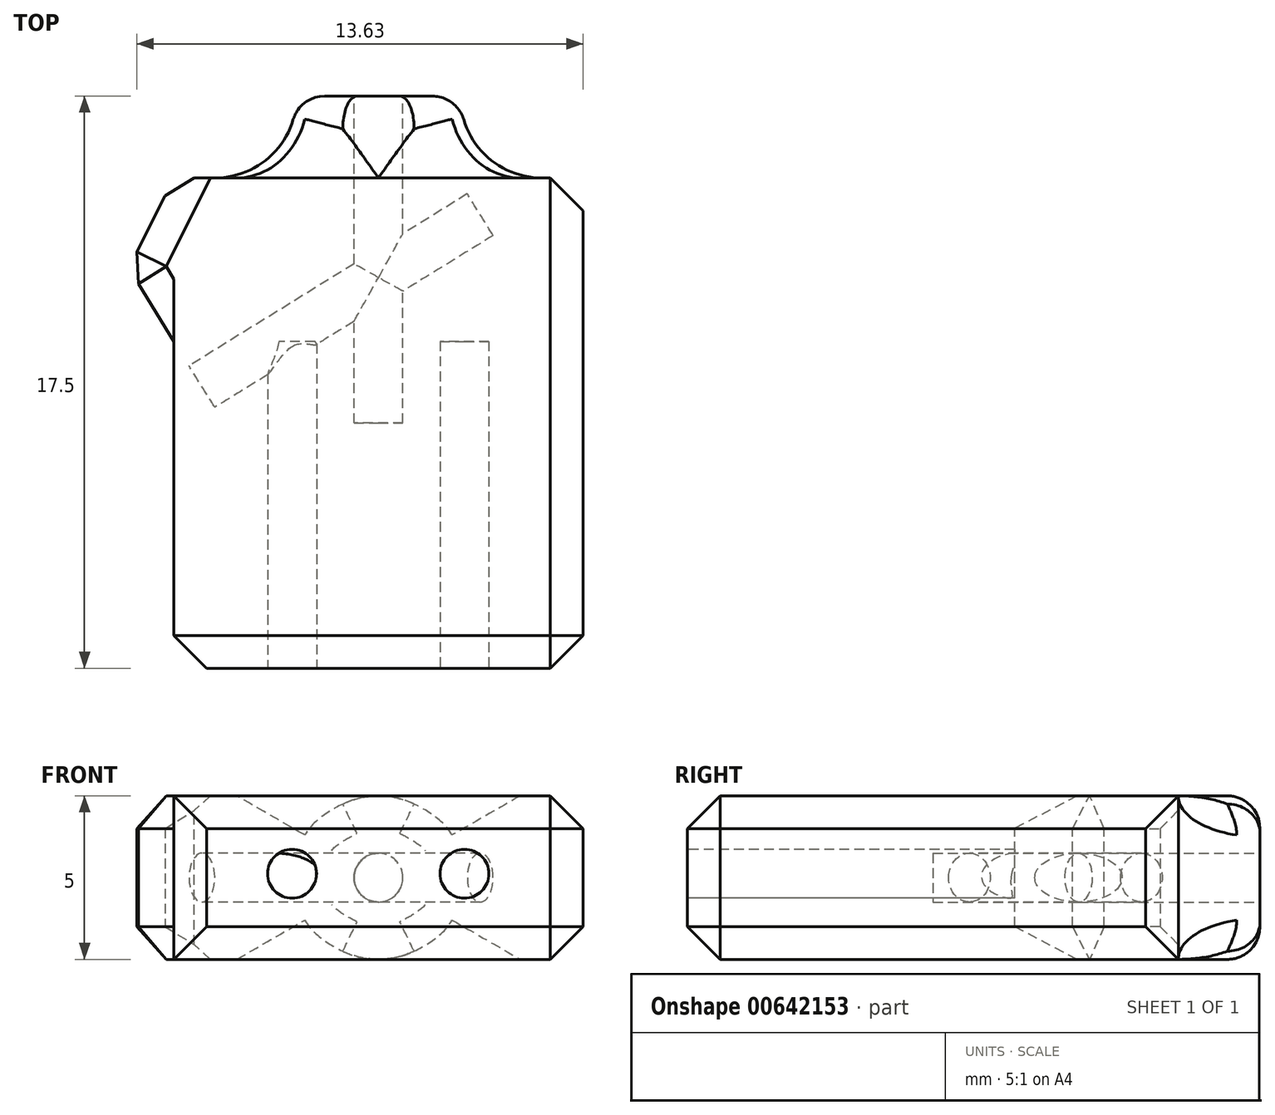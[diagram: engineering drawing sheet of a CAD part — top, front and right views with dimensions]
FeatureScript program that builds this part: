
annotation { "Feature Type Name" : "Feature", "Feature Type Description" : "" }
export const myFeature = defineFeature(function(context is Context, id is Id, definition is map)
    precondition{}
    {
        {
            var Q0;
            Q0=qCreatedBy(makeId("Top.planeOp"),FACE);
            var sketch = newSketch(context, id + "F0", { "sketchPlane" : qUnion([Q0])});
            skLineSegment(sketch, "E0.bottom", {"start": v(-3.03, 3.08) * mm, "end": v(9.47, 3.08) * mm});
            skLineSegment(sketch, "E0.top", {"start": v(-3.03, -11.92) * mm, "end": v(9.47, -11.92) * mm});
            skLineSegment(sketch, "E0.left", {"start": v(-3.03, 3.08) * mm, "end": v(-3.03, -11.92) * mm});
            skLineSegment(sketch, "E0.right", {"start": v(9.47, 3.08) * mm, "end": v(9.47, -11.92) * mm});
            skLineSegment(sketch, "E1.top", {"start": v(-3.03, -6.92) * mm, "end": v(-8.03, -6.92) * mm});
            skLineSegment(sketch, "E1.left", {"start": v(-3.03, -11.92) * mm, "end": v(-3.03, -6.92) * mm});
            skLineSegment(sketch, "E2", {"start": v(-8.03, -6.92) * mm, "end": v(-3.03, 3.08) * mm});
            skLineSegment(sketch, "E3", {"start": v(-8.03, -6.92) * mm, "end": v(-3.03, -6.92) * mm});
            skSolve(sketch);
        }
        {
            var Q0;
            Q0=makeQuery(id+"F0.imprint","IMPRINT",FACE,{"disambiguationData":[TD([[makeQuery(id+"F0.imprint","IMPRINT",EDGE,{"derivedFrom":sQuery(id+"F0.wireOp",EDGE,"E0.left")}),-1.0]])]});
            var Q1;
            Q1=makeQuery(id+"F0.imprint","IMPRINT",FACE,{"disambiguationData":[TD([[makeQuery(id+"F0.imprint","IMPRINT",EDGE,{"derivedFrom":sQuery(id+"F0.wireOp",EDGE,"E0.bottom")}),-1.0]])]});
            extrude(context, id + "F1", {"entities" : qUnion([Q0, Q1]), "depth" : 5 * mm, "offsetDistance" : 25.4 * mm});
        }
        {
            var Q0;
            Q0=makeQuery(id+"F1.opExtrude","SWEPT_EDGE",EDGE,{"disambiguationData":[OSD([sQuery(id+"F0.wireOp",EDGE,"E2"),sQuery(id+"F0.wireOp",EDGE,"E3")])]});
            chamfer(context, id + "F2", {"entities" : qUnion([Q0]), "width" : 5 * mm, "tangentPropagation" : true});
        }
        {
            var Q0;
            Q0=makeQuery(id+"F2.opChamfer","BLEND_FACE",FACE,{"disambiguationData":[OSD([sQuery(id+"F0.wireOp",EDGE,"E2"),sQuery(id+"F0.wireOp",EDGE,"E3")])]});
            var sketch = newSketch(context, id + "F3", { "sketchPlane" : qUnion([Q0])});
            skCircle(sketch, "E4", {"center": v(1.67, 2.5) * mm, "radius": 0.75 * mm});
            skPoint(sketch, "E4.centerSnap0", {"position": v(-0.96, 2.5) * mm});
            skPoint(sketch, "E4.centerSnap1", {"position": v(1.67, 0) * mm});
            skSolve(sketch);
        }
        {
            var Q0;
            Q0=makeQuery(id+"F1.opExtrude","SWEPT_FACE",FACE,{"disambiguationData":[OSD([sQuery(id+"F0.wireOp",EDGE,"E0.top")])]});
            var sketch = newSketch(context, id + "F4", { "sketchPlane" : qUnion([Q0])});
            skSolve(sketch);
        }
        {
            var Q0;
            Q0=makeQuery(id+"F1.opExtrude","SWEPT_FACE",FACE,{"disambiguationData":[OSD([sQuery(id+"F0.wireOp",EDGE,"E0.bottom")])]});
            var sketch = newSketch(context, id + "F5", { "sketchPlane" : qUnion([Q0])});
            skCircle(sketch, "E5", {"center": v(-3.22, 2.5) * mm, "radius": 2.5 * mm});
            skPoint(sketch, "E5.centerSnap0", {"position": v(-9.47, 2.5) * mm});
            skPoint(sketch, "E5.centerSnap1", {"position": v(-3.22, 5) * mm});
            skSolve(sketch);
        }
        {
            var Q0;
            {var subQ0=sQuery(id+"F5.wireOp",EDGE,"E5");var subQ1=sQuery(id+"F0.wireOp",EDGE,"E0.bottom");var subQ2=makeQuery(id+"F5.imprint","INTERSECT",VERTEX,{"derivedFrom":[makeQuery(id+"F1.opExtrude","CAP_EDGE",EDGE,{"disambiguationData":[OSD([subQ1])],"isStart":true}),subQ0]});Q0=makeQuery(id+"F5.imprint","IMPRINT",FACE,{"disambiguationData":[TD([[makeQuery(id+"F5.imprint","IMPRINT",EDGE,{"disambiguationData":[TD([[subQ2,1.0]])],"derivedFrom":subQ0}),1.0]])]});}
            extrude(context, id + "F6", {"entities" : qUnion([Q0]), "operationType" : NewBodyOperationType.ADD, "depth" : 2.5 * mm, "offsetDistance" : 25.4 * mm});
        }
        {
            var Q0;
            Q0=makeQuery(id+"F6.boolean.opBoolean","SPLIT",EDGE,{"disambiguationData":[OD(1.0)],"derivedFrom":makeQuery(id+"F6.opExtrude","CAP_EDGE",EDGE,{"disambiguationData":[OSD([sQuery(id+"F5.wireOp",EDGE,"E5")])],"isStart":true})});
            fillet(context, id + "F7", {"entities" : qUnion([Q0]), "radius" : 2.5 * mm, "tangentPropagation" : true, "allowEdgeOverflow" : false});
        }
        {
            var Q0;
            Q0=makeQuery(id+"F6.opExtrude","CAP_EDGE",EDGE,{"disambiguationData":[OSD([sQuery(id+"F5.wireOp",EDGE,"E5")])],"isStart":false});
            var Q1;
            {var subQ0=sQuery(id+"F5.wireOp",EDGE,"E5");Q1=makeQuery(id+"F7.opFillet","BLEND_EDGE",EDGE,{"blendedFrom":[makeQuery(id+"F6.boolean.opBoolean","SPLIT",EDGE,{"disambiguationData":[OD(1.0)],"derivedFrom":makeQuery(id+"F6.opExtrude","CAP_EDGE",EDGE,{"disambiguationData":[OSD([subQ0])],"isStart":true})}),makeQuery(id+"F6.opExtrude","CAP_FACE",FACE,{"disambiguationData":[OSD([subQ0])],"isStart":false})],"blendedInto":[makeQuery(id+"F6.opExtrude","CAP_FACE",FACE,{"disambiguationData":[OSD([subQ0])],"isStart":false})]});}
            var Q2;
            {var subQ0=sQuery(id+"F5.wireOp",EDGE,"E5");Q2=makeQuery(id+"F7.opFillet","BLEND_EDGE",EDGE,{"blendedFrom":[makeQuery(id+"F6.boolean.opBoolean","SPLIT",EDGE,{"disambiguationData":[OD(0.0)],"derivedFrom":makeQuery(id+"F6.opExtrude","CAP_EDGE",EDGE,{"disambiguationData":[OSD([subQ0])],"isStart":true})}),makeQuery(id+"F6.opExtrude","CAP_FACE",FACE,{"disambiguationData":[OSD([subQ0])],"isStart":false})],"blendedInto":[makeQuery(id+"F6.opExtrude","CAP_FACE",FACE,{"disambiguationData":[OSD([subQ0])],"isStart":false})]});}
            fillet(context, id + "F8", {"entities" : qUnion([Q0, Q1, Q2]), "radius" : 1 * mm, "tangentPropagation" : true, "allowEdgeOverflow" : false});
        }
        {
            var Q0;
            Q0=makeQuery(id+"F6.opExtrude","CAP_FACE",FACE,{"disambiguationData":[OSD([sQuery(id+"F5.wireOp",EDGE,"E5")])],"isStart":false});
            var sketch = newSketch(context, id + "F9", { "sketchPlane" : qUnion([Q0])});
            skCircle(sketch, "E6", {"center": v(-3.22, 2.5) * mm, "radius": 0.75 * mm});
            skSolve(sketch);
        }
        {
            var Q0;
            Q0=makeQuery(id+"F3.imprint","IMPRINT",FACE,{"disambiguationData":[TD([[makeQuery(id+"F3.imprint","IMPRINT",EDGE,{"derivedFrom":sQuery(id+"F3.wireOp",EDGE,"E4")}),1.0]])]});
            var Q1;
            Q1=sQuery(id+"F3.wireOp",EDGE,"E4");
            extrude(context, id + "F10", {"entities" : qUnion([Q0]), "operationType" : NewBodyOperationType.REMOVE, "surfaceEntities" : qUnion([Q1]), "oppositeDirection" : true, "depth" : 10 * mm, "offsetDistance" : 25.4 * mm});
        }
        {
            var Q0;
            Q0=makeQuery(id+"F1.opExtrude","CAP_EDGE",EDGE,{"disambiguationData":[OSD([sQuery(id+"F0.wireOp",EDGE,"E0.top")])],"isStart":false});
            var Q1;
            Q1=makeQuery(id+"F1.opExtrude","CAP_EDGE",EDGE,{"disambiguationData":[OSD([sQuery(id+"F0.wireOp",EDGE,"E0.right")])],"isStart":false});
            var Q2;
            Q2=makeQuery(id+"F2.opChamfer","BLEND_EDGE",EDGE,{"blendedFrom":[makeQuery(id+"F1.opExtrude","SWEPT_EDGE",EDGE,{"disambiguationData":[OSD([sQuery(id+"F0.wireOp",EDGE,"E2"),sQuery(id+"F0.wireOp",EDGE,"E3")])]}),makeQuery(id+"F1.opExtrude","SWEPT_FACE",FACE,{"disambiguationData":[OSD([sQuery(id+"F0.wireOp",EDGE,"E1.left")])]})],"blendedInto":[makeQuery(id+"F1.opExtrude","SWEPT_FACE",FACE,{"disambiguationData":[OSD([sQuery(id+"F0.wireOp",EDGE,"E1.left")])]})]});
            var Q3;
            {var subQ0=sQuery(id+"F0.wireOp",EDGE,"E2");Q3=makeQuery(id+"F2.opChamfer","BLEND_EDGE",EDGE,{"blendedFrom":[makeQuery(id+"F1.opExtrude","SWEPT_EDGE",EDGE,{"disambiguationData":[OSD([subQ0,sQuery(id+"F0.wireOp",EDGE,"E3")])]}),makeQuery(id+"F1.opExtrude","SWEPT_FACE",FACE,{"disambiguationData":[OSD([subQ0])]})],"blendedInto":[makeQuery(id+"F1.opExtrude","SWEPT_FACE",FACE,{"disambiguationData":[OSD([subQ0])]})]});}
            var Q4;
            {var subQ0=sQuery(id+"F0.wireOp",EDGE,"E3");var subQ1=sQuery(id+"F0.wireOp",EDGE,"E2");Q4=makeQuery(id+"F2.opChamfer","BLEND_EDGE",EDGE,{"blendedFrom":[makeQuery(id+"F1.opExtrude","SWEPT_EDGE",EDGE,{"disambiguationData":[OSD([subQ1,subQ0])]}),makeQuery(id+"F1.opExtrude","CAP_FACE",FACE,{"disambiguationData":[OSD([sQuery(id+"F0.wireOp",EDGE,"E0.bottom"),sQuery(id+"F0.wireOp",EDGE,"E0.top"),sQuery(id+"F0.wireOp",EDGE,"E0.right"),sQuery(id+"F0.wireOp",EDGE,"E1.left"),subQ1,subQ0])],"isStart":false})],"blendedInto":[makeQuery(id+"F1.opExtrude","CAP_FACE",FACE,{"disambiguationData":[OSD([sQuery(id+"F0.wireOp",EDGE,"E0.bottom"),sQuery(id+"F0.wireOp",EDGE,"E0.top"),sQuery(id+"F0.wireOp",EDGE,"E0.right"),sQuery(id+"F0.wireOp",EDGE,"E1.left"),subQ1,subQ0])],"isStart":false})]});}
            var Q5;
            {var subQ0=sQuery(id+"F0.wireOp",EDGE,"E3");var subQ1=sQuery(id+"F0.wireOp",EDGE,"E2");Q5=makeQuery(id+"F2.opChamfer","BLEND_EDGE",EDGE,{"blendedFrom":[makeQuery(id+"F1.opExtrude","SWEPT_EDGE",EDGE,{"disambiguationData":[OSD([subQ1,subQ0])]}),makeQuery(id+"F1.opExtrude","CAP_FACE",FACE,{"disambiguationData":[OSD([sQuery(id+"F0.wireOp",EDGE,"E0.bottom"),sQuery(id+"F0.wireOp",EDGE,"E0.top"),sQuery(id+"F0.wireOp",EDGE,"E0.right"),sQuery(id+"F0.wireOp",EDGE,"E1.left"),subQ1,subQ0])],"isStart":true})],"blendedInto":[makeQuery(id+"F1.opExtrude","CAP_FACE",FACE,{"disambiguationData":[OSD([sQuery(id+"F0.wireOp",EDGE,"E0.bottom"),sQuery(id+"F0.wireOp",EDGE,"E0.top"),sQuery(id+"F0.wireOp",EDGE,"E0.right"),sQuery(id+"F0.wireOp",EDGE,"E1.left"),subQ1,subQ0])],"isStart":true})]});}
            var Q6;
            Q6=makeQuery(id+"F1.opExtrude","CAP_EDGE",EDGE,{"disambiguationData":[OSD([sQuery(id+"F0.wireOp",EDGE,"E2")])],"isStart":true});
            var Q7;
            Q7=makeQuery(id+"F1.opExtrude","CAP_EDGE",EDGE,{"disambiguationData":[OSD([sQuery(id+"F0.wireOp",EDGE,"E2")])],"isStart":false});
            var Q8;
            Q8=makeQuery(id+"F1.opExtrude","SWEPT_EDGE",EDGE,{"disambiguationData":[OSD([sQuery(id+"F0.wireOp",EDGE,"E0.bottom"),sQuery(id+"F0.wireOp",EDGE,"E0.left"),sQuery(id+"F0.wireOp",EDGE,"E2")])]});
            var Q9;
            Q9=makeQuery(id+"F1.opExtrude","SWEPT_EDGE",EDGE,{"disambiguationData":[OSD([sQuery(id+"F0.wireOp",EDGE,"E0.top"),sQuery(id+"F0.wireOp",EDGE,"E1.left")])]});
            var Q10;
            Q10=makeQuery(id+"F1.opExtrude","SWEPT_EDGE",EDGE,{"disambiguationData":[OSD([sQuery(id+"F0.wireOp",EDGE,"E0.top"),sQuery(id+"F0.wireOp",EDGE,"E0.right")])]});
            var Q11;
            Q11=makeQuery(id+"F1.opExtrude","CAP_EDGE",EDGE,{"disambiguationData":[OSD([sQuery(id+"F0.wireOp",EDGE,"E0.right")])],"isStart":true});
            var Q12;
            Q12=makeQuery(id+"F1.opExtrude","CAP_EDGE",EDGE,{"disambiguationData":[OSD([sQuery(id+"F0.wireOp",EDGE,"E0.top")])],"isStart":true});
            var Q13;
            Q13=makeQuery(id+"F1.opExtrude","SWEPT_EDGE",EDGE,{"disambiguationData":[OSD([sQuery(id+"F0.wireOp",EDGE,"E0.bottom"),sQuery(id+"F0.wireOp",EDGE,"E0.right")])]});
            chamfer(context, id + "F11", {"entities" : qUnion([Q0, Q1, Q2, Q3, Q4, Q5, Q6, Q7, Q8, Q9, Q10, Q11, Q12, Q13]), "width" : 1 * mm, "tangentPropagation" : true});
        }
        {
            var Q0;
            {var subQ0=sQuery(id+"F0.wireOp",EDGE,"E0.top");Q0=makeQuery(id+"F4.imprint","IMPRINT",FACE,{"disambiguationData":[TD([[makeQuery(id+"F4.imprint","IMPRINT",EDGE,{"derivedFrom":makeQuery(id+"F1.opExtrude","CAP_EDGE",EDGE,{"disambiguationData":[OSD([subQ0])],"isStart":true})}),1.0]])]});}
            var sketch = newSketch(context, id + "F12", { "sketchPlane" : qUnion([Q0])});
            skCircle(sketch, "E7", {"center": v(0.58, 2.62) * mm, "radius": 0.75 * mm});
            skCircle(sketch, "E8", {"center": v(5.85, 2.62) * mm, "radius": 0.75 * mm});
            skSolve(sketch);
        }
        {
            var Q0;
            Q0 = qSketchRegion(id + "F12", true);
            extrude(context, id + "F13", {"entities" : qUnion([Q0]), "operationType" : NewBodyOperationType.REMOVE, "oppositeDirection" : true, "depth" : 10 * mm, "offsetDistance" : 25.4 * mm});
        }
        {
            var Q0;
            Q0=makeQuery(id+"F9.imprint","IMPRINT",FACE,{"disambiguationData":[TD([[makeQuery(id+"F9.imprint","IMPRINT",EDGE,{"derivedFrom":sQuery(id+"F9.wireOp",EDGE,"E6")}),1.0]])]});
            extrude(context, id + "F14", {"entities" : qUnion([Q0]), "operationType" : NewBodyOperationType.REMOVE, "oppositeDirection" : true, "depth" : 10 * mm, "offsetDistance" : 25.4 * mm});
        }
    });
